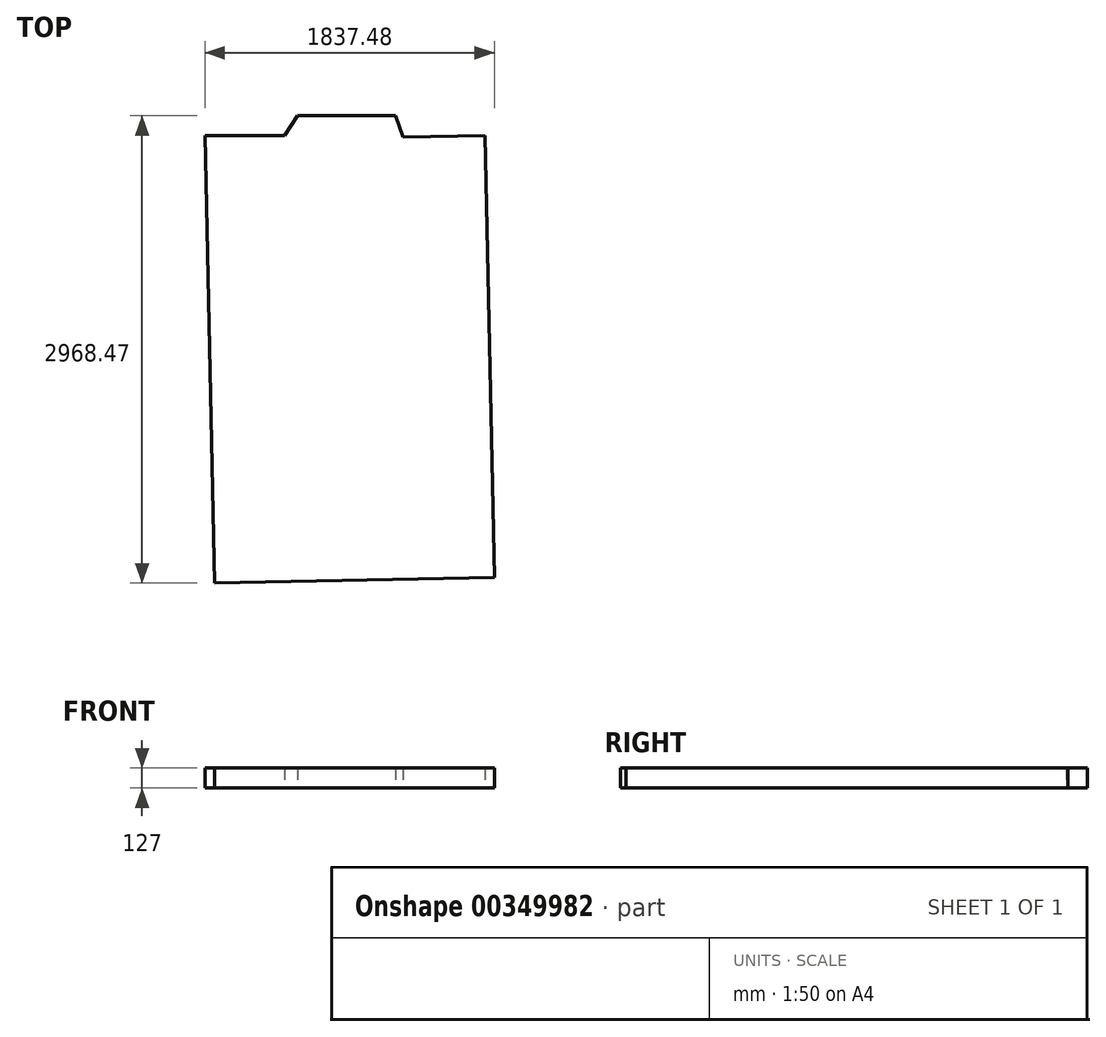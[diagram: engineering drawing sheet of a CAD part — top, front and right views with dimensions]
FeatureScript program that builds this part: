
annotation { "Feature Type Name" : "Feature", "Feature Type Description" : "" }
export const myFeature = defineFeature(function(context is Context, id is Id, definition is map)
    precondition{}
    {
        {
            var Q0;
            Q0=qCreatedBy(makeId("Top.planeOp"),FACE);
            var sketch = newSketch(context, id + "F0", { "sketchPlane" : qUnion([Q0])});
            skLineSegment(sketch, "E0", {"start": v(-40.27, 45.9) * mm, "end": v(19.6, -2798.27) * mm});
            skLineSegment(sketch, "E1", {"start": v(19.6, -2798.27) * mm, "end": v(1797.21, -2760.85) * mm});
            skLineSegment(sketch, "E2", {"start": v(1797.21, -2760.85) * mm, "end": v(1738.12, 45.9) * mm});
            skLineSegment(sketch, "E3", {"start": v(1738.12, 45.9) * mm, "end": v(1216.32, 34.9) * mm});
            skLineSegment(sketch, "E4", {"start": v(1216.32, 34.9) * mm, "end": v(1170.94, 170.2) * mm});
            skLineSegment(sketch, "E5", {"start": v(1170.94, 170.2) * mm, "end": v(549.07, 170.2) * mm});
            skLineSegment(sketch, "E6", {"start": v(549.07, 170.2) * mm, "end": v(464.64, 45.9) * mm});
            skLineSegment(sketch, "E7", {"start": v(464.64, 45.9) * mm, "end": v(-40.27, 45.9) * mm});
            skSolve(sketch);
        }
        {
            var Q0;
            Q0 = qSketchRegion(id + "F0", true);
            extrude(context, id + "F1", {"entities" : qUnion([Q0]), "depth" : 127 * mm, "offsetDistance" : 25 * mm});
        }
    });
